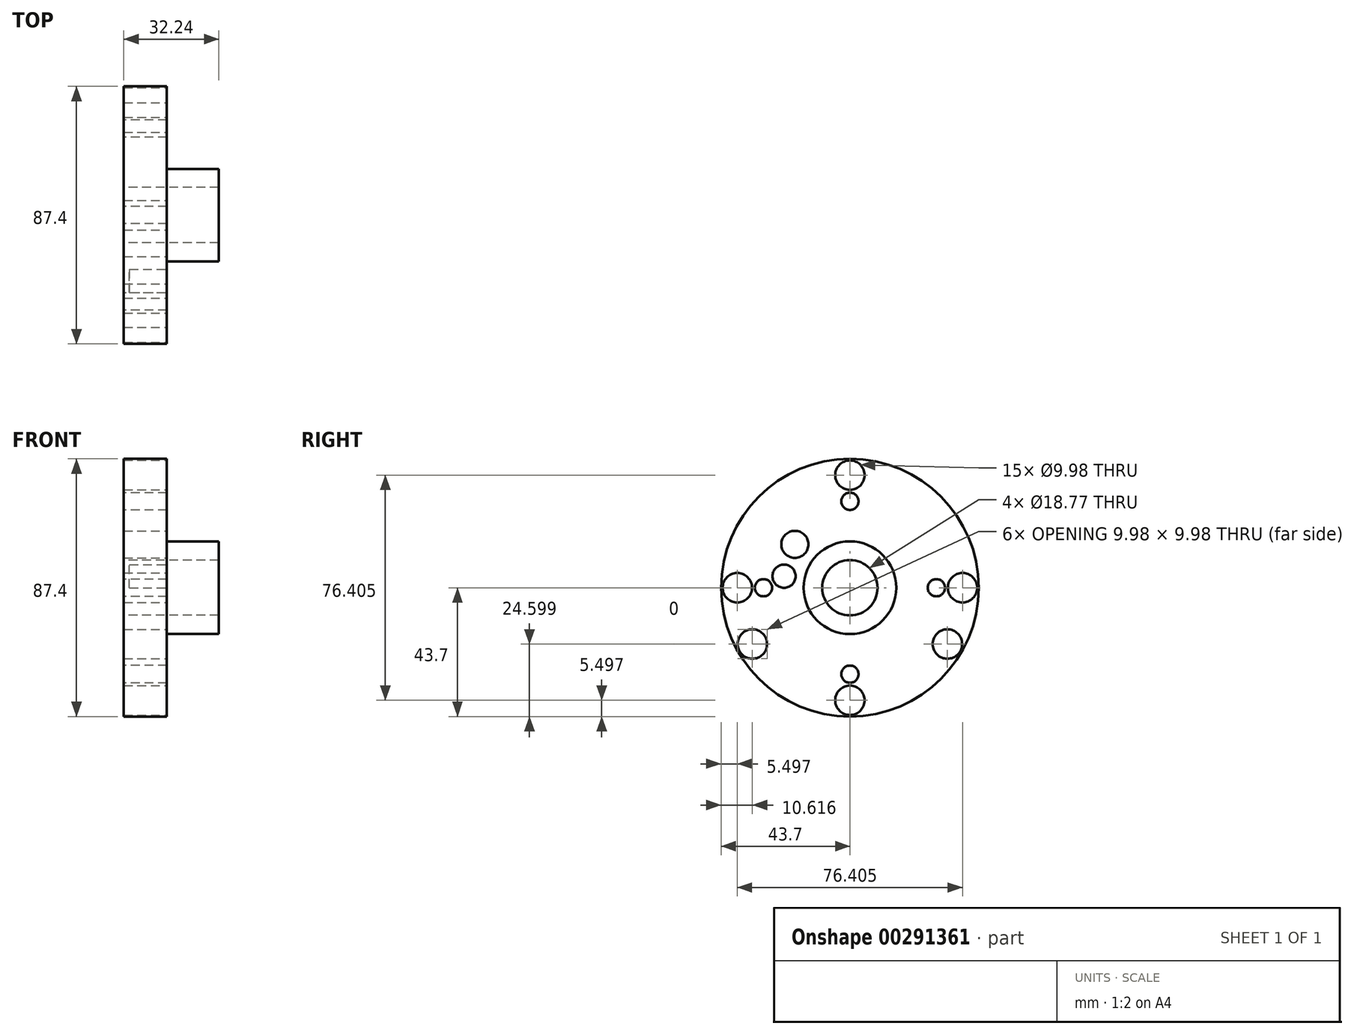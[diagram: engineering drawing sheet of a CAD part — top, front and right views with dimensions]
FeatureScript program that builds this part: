
annotation { "Feature Type Name" : "Feature", "Feature Type Description" : "" }
export const myFeature = defineFeature(function(context is Context, id is Id, definition is map)
    precondition{}
    {
        {
            var Q0;
            Q0=qCreatedBy(makeId("Front.planeOp"),FACE);
            var sketch = newSketch(context, id + "F0", { "sketchPlane" : qUnion([Q0])});
            skLineSegment(sketch, "E0", {"start": v(0, 43.7) * mm, "end": v(14.64, 43.7) * mm});
            skLineSegment(sketch, "E1", {"start": v(14.64, 43.7) * mm, "end": v(14.64, 15.72) * mm});
            skLineSegment(sketch, "E2", {"start": v(14.64, 15.72) * mm, "end": v(32.24, 15.72) * mm});
            skLineSegment(sketch, "E3", {"start": v(32.24, 15.72) * mm, "end": v(32.24, 9.38) * mm});
            skLineSegment(sketch, "E4", {"start": v(32.24, 9.38) * mm, "end": v(14.64, 9.38) * mm});
            skLineSegment(sketch, "E5", {"start": v(14.64, 9.38) * mm, "end": v(0, 9.38) * mm});
            skLineSegment(sketch, "E6", {"start": v(0, 9.38) * mm, "end": v(0, 43.7) * mm});
            skLineSegment(sketch, "E7", {"start": v(-132.54, 0) * mm, "end": v(195.75, 0) * mm, "construction": true});
            skSolve(sketch);
        }
        {
            var Q0;
            Q0=makeQuery(id+"F0.imprint","IMPRINT",FACE,{"disambiguationData":[TD([[makeQuery(id+"F0.imprint","IMPRINT",EDGE,{"derivedFrom":sQuery(id+"F0.wireOp",EDGE,"E0")}),-1.0]])]});
            var Q1;
            Q1=sQuery(id+"F0.wireOp",EDGE,"E7");
            revolve(context, id + "F1", {"entities" : qUnion([Q0]), "axis" : qUnion([Q1]), "revolveType" : RevolveType.FULL});
        }
        {
            var Q0;
            Q0=makeQuery(id+"F1.opRevolve","SWEPT_FACE",FACE,{"disambiguationData":[OSD([sQuery(id+"F0.wireOp",EDGE,"E1")])]});
            var sketch = newSketch(context, id + "F2", { "sketchPlane" : qUnion([Q0])});
            skCircle(sketch, "E8", {"center": v(0, 0) * mm, "radius": 31.75 * mm, "construction": true});
            skSolve(sketch);
        }
        {
            var Q0;
            {var subQ0=sQuery(id+"F0.wireOp",EDGE,"E1");Q0=makeQuery(id+"F2.imprint","IMPRINT",FACE,{"disambiguationData":[TD([[makeQuery(id+"F2.imprint","IMPRINT",EDGE,{"derivedFrom":makeQuery(id+"F1.opRevolve","SWEPT_EDGE",EDGE,{"disambiguationData":[OSD([sQuery(id+"F0.wireOp",EDGE,"E0"),subQ0])]})}),-1.0]])]});}
            var sketch = newSketch(context, id + "F3", { "sketchPlane" : qUnion([Q0])});
            skCircle(sketch, "E9", {"center": v(0, 38.2) * mm, "radius": 5 * mm});
            skSolve(sketch);
        }
        {
            var Q0;
            Q0=makeQuery(id+"F1.opRevolve","SWEPT_FACE",FACE,{"disambiguationData":[OSD([sQuery(id+"F0.wireOp",EDGE,"E6")])]});
            var sketch = newSketch(context, id + "F4", { "sketchPlane" : qUnion([Q0])});
            skCircle(sketch, "E10", {"center": v(0, 0) * mm, "radius": 29.32 * mm});
            skCircle(sketch, "E11", {"center": v(0, 0) * mm, "radius": 25.35 * mm, "construction": true});
            skCircle(sketch, "E12", {"center": v(0, 29.32) * mm, "radius": 2.93 * mm});
            skCircle(sketch, "E13", {"center": v(0, 25.35) * mm, "radius": 2.3 * mm});
            skSolve(sketch);
        }
        {
            var Q0;
            {var subQ0=sQuery(id+"F4.wireOp",EDGE,"E12");var subQ1=sQuery(id+"F4.wireOp",EDGE,"E10");var subQ2=makeQuery(id+"F4.imprint","INTERSECT",VERTEX,{"disambiguationData":[OD(0.0)],"derivedFrom":[subQ1,subQ0]});Q0=makeQuery(id+"F4.imprint","IMPRINT",FACE,{"disambiguationData":[TD([[makeQuery(id+"F4.imprint","IMPRINT",EDGE,{"disambiguationData":[TD([[subQ2,1.0]])],"derivedFrom":subQ1}),1.0]])]});}
            var Q1;
            {var subQ0=sQuery(id+"F4.wireOp",EDGE,"E12");var subQ1=sQuery(id+"F4.wireOp",EDGE,"E10");var subQ2=makeQuery(id+"F4.imprint","INTERSECT",VERTEX,{"disambiguationData":[OD(0.0)],"derivedFrom":[subQ1,subQ0]});Q1=makeQuery(id+"F4.imprint","IMPRINT",FACE,{"disambiguationData":[TD([[makeQuery(id+"F4.imprint","IMPRINT",EDGE,{"disambiguationData":[TD([[subQ2,1.0]])],"derivedFrom":subQ1}),-1.0]])]});}
            var Q2;
            {var subQ0=sQuery(id+"F4.wireOp",EDGE,"E13");var subQ1=sQuery(id+"F4.wireOp",EDGE,"E12");var subQ2=makeQuery(id+"F4.imprint","INTERSECT",VERTEX,{"disambiguationData":[OD(0.0)],"derivedFrom":[subQ1,subQ0]});Q2=makeQuery(id+"F4.imprint","IMPRINT",FACE,{"disambiguationData":[TD([[makeQuery(id+"F4.imprint","IMPRINT",EDGE,{"disambiguationData":[TD([[subQ2,-1.0]])],"derivedFrom":subQ1}),1.0]])]});}
            var Q3;
            Q3=sQuery(id+"F4.wireOp",EDGE,"E12");
            extrude(context, id + "F5", {"entities" : qUnion([Q0, Q1, Q2]), "operationType" : NewBodyOperationType.REMOVE, "surfaceEntities" : qUnion([Q3]), "endBound" : BoundingType.SYMMETRIC, "oppositeDirection" : true, "depth" : 127 * mm});
        }
        {
            var Q0;
            Q0=makeQuery(id+"F3.imprint","IMPRINT",FACE,{"disambiguationData":[TD([[makeQuery(id+"F3.imprint","IMPRINT",EDGE,{"derivedFrom":sQuery(id+"F3.wireOp",EDGE,"E9")}),-1.0]])]});
            var sketch = newSketch(context, id + "F6", { "sketchPlane" : qUnion([Q0])});
            skSolve(sketch);
        }
        {
            var Q0;
            Q0=makeQuery(id+"F6.imprint","IMPRINT",FACE,{"disambiguationData":[TD([[makeQuery(id+"F6.imprint","IMPRINT",EDGE,{"derivedFrom":makeQuery(id+"F3.imprint","IMPRINT",EDGE,{"derivedFrom":sQuery(id+"F3.wireOp",EDGE,"E9")})}),1.0]])]});
            extrude(context, id + "F7", {"entities" : qUnion([Q0]), "operationType" : NewBodyOperationType.REMOVE, "oppositeDirection" : true, "depth" : 25.4 * mm});
        }
        {
            var Q0;
            Q0=makeQuery(id+"F1.opRevolve","SWEPT_BODY",BODY,{"disambiguationData":[OSD([sQuery(id+"F0.wireOp",EDGE,"E0"),sQuery(id+"F0.wireOp",EDGE,"E1"),sQuery(id+"F0.wireOp",EDGE,"E2"),sQuery(id+"F0.wireOp",EDGE,"E3"),sQuery(id+"F0.wireOp",EDGE,"E4"),sQuery(id+"F0.wireOp",EDGE,"E5"),sQuery(id+"F0.wireOp",EDGE,"E6")])]});
            var Q1;
            Q1=makeQuery(id+"F1.opRevolve","SWEPT_EDGE",EDGE,{"disambiguationData":[OSD([sQuery(id+"F0.wireOp",EDGE,"E5"),sQuery(id+"F0.wireOp",EDGE,"E6")])]});
            circularPattern(context, id + "F8", {"entities" : qUnion([Q0]), "axis" : qUnion([Q1]), "angle" : 360 * degree, "instanceCount" : 4, "equalSpace" : true});
        }
        {
            var Q0;
            Q0 = qSketchRegion(id + "F3", true);
            extrude(context, id + "F9", {"entities" : qUnion([Q0]), "depth" : 25.4 * mm});
        }
        {
            var Q0;
            Q0=makeQuery(id+"F9.opExtrude","SWEPT_BODY",BODY,{"disambiguationData":[OSD([sQuery(id+"F3.wireOp",EDGE,"E9")])]});
            var Q1;
            Q1=makeQuery(id+"F1.opRevolve","SWEPT_EDGE",EDGE,{"disambiguationData":[OSD([sQuery(id+"F0.wireOp",EDGE,"E3"),sQuery(id+"F0.wireOp",EDGE,"E4")])]});
            circularPattern(context, id + "F10", {"entities" : qUnion([Q0]), "axis" : qUnion([Q1]), "angle" : 360 * degree, "instanceCount" : 3, "equalSpace" : true});
        }
        {
            var Q0;
            {var subQ0=sQuery(id+"F0.wireOp",EDGE,"E1");Q0=makeQuery(id+"F2.imprint","IMPRINT",FACE,{"disambiguationData":[TD([[makeQuery(id+"F2.imprint","IMPRINT",EDGE,{"derivedFrom":makeQuery(id+"F1.opRevolve","SWEPT_EDGE",EDGE,{"disambiguationData":[OSD([sQuery(id+"F0.wireOp",EDGE,"E0"),subQ0])]})}),-1.0]])]});}
            var sketch = newSketch(context, id + "F11", { "sketchPlane" : qUnion([Q0])});
            skCircle(sketch, "E14", {"center": v(0, 0) * mm, "radius": 22.69 * mm, "construction": true});
            skCircle(sketch, "E15", {"center": v(-22.35, 3.91) * mm, "radius": 3.92 * mm});
            skSolve(sketch);
        }
        {
            var Q0;
            Q0 = qSketchRegion(id + "F11", true);
            extrude(context, id + "F12", {"entities" : qUnion([Q0]), "operationType" : NewBodyOperationType.REMOVE, "endBound" : BoundingType.SYMMETRIC, "oppositeDirection" : true, "depth" : 25.4 * mm});
        }
        {
            var Q0;
            {var subQ0=sQuery(id+"F0.wireOp",EDGE,"E1");Q0=makeQuery(id+"F2.imprint","IMPRINT",FACE,{"disambiguationData":[TD([[makeQuery(id+"F2.imprint","IMPRINT",EDGE,{"derivedFrom":makeQuery(id+"F1.opRevolve","SWEPT_EDGE",EDGE,{"disambiguationData":[OSD([sQuery(id+"F0.wireOp",EDGE,"E0"),subQ0])]})}),-1.0]])]});}
            var sketch = newSketch(context, id + "F13", { "sketchPlane" : qUnion([Q0])});
            skCircle(sketch, "E16", {"center": v(0, 0) * mm, "radius": 23.78 * mm, "construction": true});
            skCircle(sketch, "E17", {"center": v(-18.68, 14.72) * mm, "radius": 4.59 * mm});
            skSolve(sketch);
        }
        {
            var Q0;
            Q0 = qSketchRegion(id + "F13", true);
            extrude(context, id + "F14", {"entities" : qUnion([Q0]), "operationType" : NewBodyOperationType.REMOVE, "endBound" : BoundingType.SYMMETRIC, "oppositeDirection" : true, "depth" : 76.2 * mm});
        }
        {
            var Q0;
            Q0=makeQuery(id+"F10.opPattern","COPY",FACE,{"derivedFrom":makeQuery(id+"F9.opExtrude","CAP_FACE",FACE,{"disambiguationData":[OSD([sQuery(id+"F3.wireOp",EDGE,"E9")])],"isStart":false}),"instanceName":"1"});
            var sketch = newSketch(context, id + "F15", { "sketchPlane" : qUnion([Q0])});
            skSolve(sketch);
        }
        {
            var Q0;
            Q0=makeQuery(id+"F10.opPattern","COPY",FACE,{"derivedFrom":makeQuery(id+"F9.opExtrude","CAP_FACE",FACE,{"disambiguationData":[OSD([sQuery(id+"F3.wireOp",EDGE,"E9")])],"isStart":false}),"instanceName":"2"});
            var Q1;
            Q1=makeQuery(id+"F9.opExtrude","CAP_FACE",FACE,{"disambiguationData":[OSD([sQuery(id+"F3.wireOp",EDGE,"E9")])],"isStart":false});
            var Q2;
            Q2=makeQuery(id+"F15.imprint","IMPRINT",FACE,{"disambiguationData":[TD([[makeQuery(id+"F15.imprint","IMPRINT",EDGE,{"derivedFrom":makeQuery(id+"F10.opPattern","COPY",EDGE,{"derivedFrom":makeQuery(id+"F9.opExtrude","CAP_EDGE",EDGE,{"disambiguationData":[OSD([sQuery(id+"F3.wireOp",EDGE,"E9")])],"isStart":false}),"instanceName":"1"})}),1.0]])]});
            extrude(context, id + "F16", {"entities" : qUnion([Q0, Q1, Q2]), "operationType" : NewBodyOperationType.REMOVE, "oppositeDirection" : true, "depth" : 127 * mm});
        }
    });
